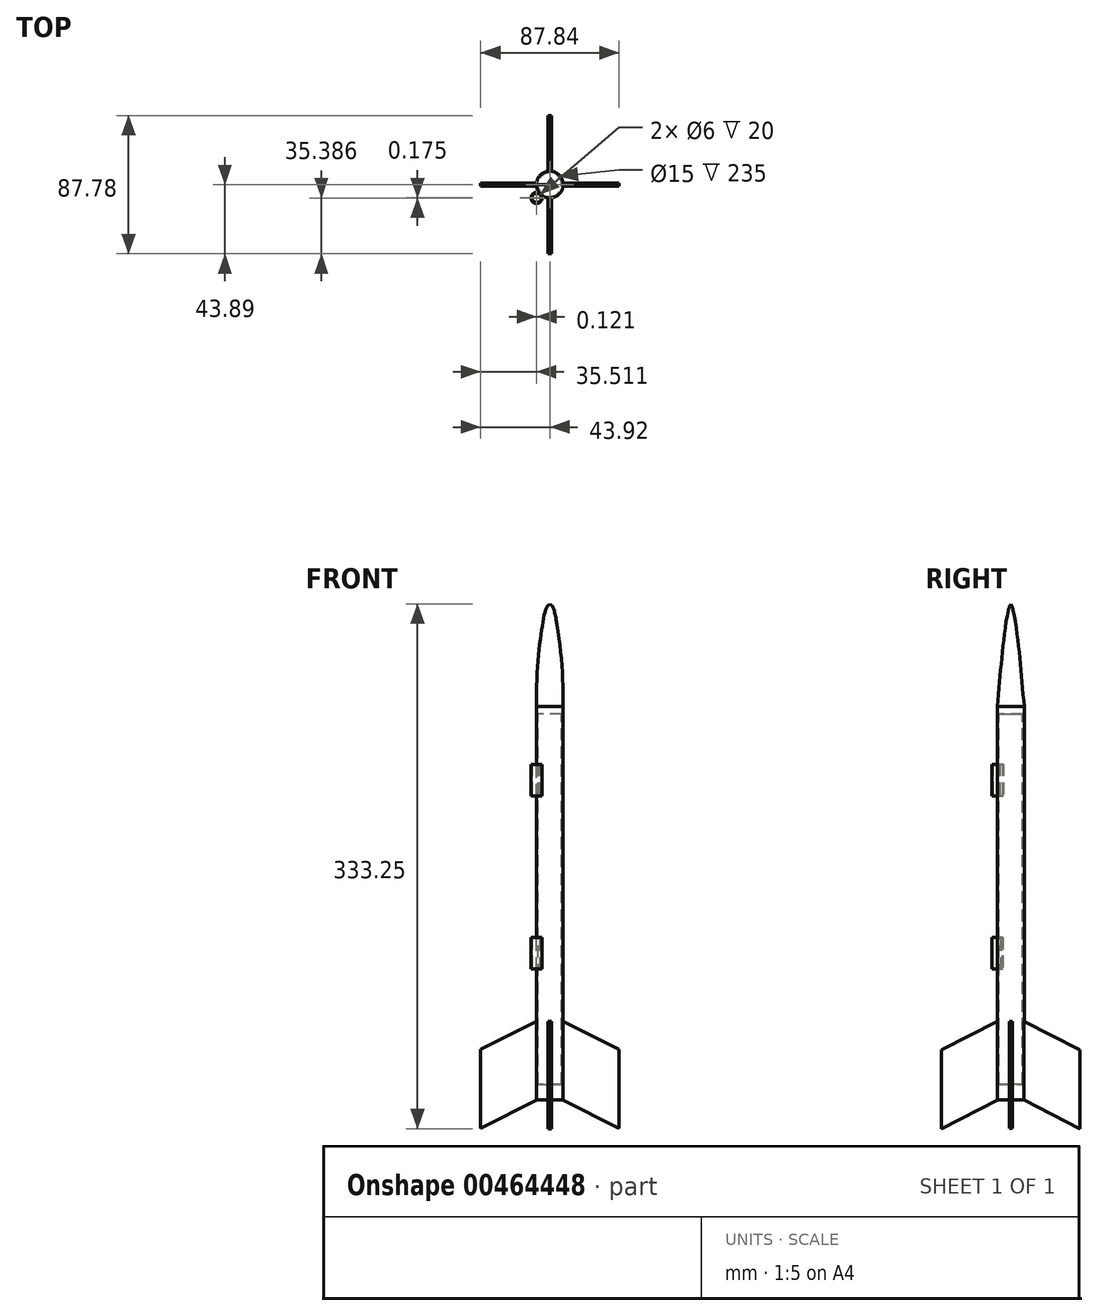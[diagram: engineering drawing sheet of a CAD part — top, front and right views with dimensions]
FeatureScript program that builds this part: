
annotation { "Feature Type Name" : "Feature", "Feature Type Description" : "" }
export const myFeature = defineFeature(function(context is Context, id is Id, definition is map)
    precondition{}
    {
        {
            var Q0;
            Q0=qCreatedBy(makeId("Front.planeOp"),FACE);
            var sketch = newSketch(context, id + "F0", { "sketchPlane" : qUnion([Q0])});
            skLineSegment(sketch, "E0", {"start": v(0, 0) * mm, "end": v(0, 70) * mm});
            skLineSegment(sketch, "E1", {"start": v(0, 0) * mm, "end": v(7.5, 0) * mm});
            skLineSegment(sketch, "E2", {"start": v(7.5, 0) * mm, "end": v(7.5, 5) * mm});
            skLineSegment(sketch, "E3", {"start": v(7.5, 5) * mm, "end": v(8.5, 5) * mm});
            skFitSpline(sketch, "E4", {"points": [v(0, 70) * mm, v(3.74, 61.8) * mm, v(8.5, 5) * mm], "startDerivative": vector(22.14, -9.96) * mm, "endDerivative": vector(-1.28, -102.15) * mm});
            skFitSpline(sketch, "E5.MirrorCS", {"points": [v(0, 70) * mm, v(-3.74, 61.8) * mm, v(-8.5, 5) * mm], "startDerivative": vector(-22.14, -9.96) * mm, "endDerivative": vector(1.28, -102.15) * mm});
            skLineSegment(sketch, "E6.MirrorCS", {"start": v(-7.5, 5) * mm, "end": v(-8.5, 5) * mm});
            skLineSegment(sketch, "E7.MirrorCS", {"start": v(-7.5, 0) * mm, "end": v(-7.5, 5) * mm});
            skLineSegment(sketch, "E8.MirrorCS", {"start": v(0, 0) * mm, "end": v(-7.5, 0) * mm});
            skSolve(sketch);
        }
        {
            var Q0;
            Q0=sQuery(id+"F0.wireOp",EDGE,"E3");
            cPlane(context, id + "F1", {"entities" : qUnion([Q0]), "cplaneType" : CPlaneType.LINE_ANGLE, "offset" : 25 * mm, "angle" : 90 * degree, "width" : 150 * mm, "height" : 150 * mm});
        }
        {
            var Q0;
            Q0=qCreatedBy(id+"F1.planeOp",FACE);
            var sketch = newSketch(context, id + "F2", { "sketchPlane" : qUnion([Q0])});
            skCircle(sketch, "E9", {"center": v(0, 0) * mm, "radius": 8.5 * mm});
            skSolve(sketch);
        }
        {
            var Q0;
            Q0=makeQuery(id+"F2.imprint","IMPRINT",FACE,{"disambiguationData":[TD([[makeQuery(id+"F2.imprint","IMPRINT",EDGE,{"derivedFrom":sQuery(id+"F2.wireOp",EDGE,"E9")}),1.0]])]});
            var Q1;
            Q1=sQuery(id+"F0.wireOp",VERTEX,"E5.MirrorCS.0.internal");
            var Q2;
            Q2=sQuery(id+"F0.wireOp",EDGE,"E4");
            var Q3;
            Q3=sQuery(id+"F0.wireOp",EDGE,"E5.MirrorCS");
            loft(context, id + "F3", {"addGuides" : true, "sheetProfilesArray" : [{ "sheetProfileEntities" : qUnion([Q0]) }, { "sheetProfileEntities" : qUnion([Q1]) }], "guidesArray" : [{ "guideEntities" : qUnion([Q2]), "guideDerivativeType" : LoftGuideDerivativeType.DEFAULT, "guideDerivativeMagnitude" : 1 }, { "guideEntities" : qUnion([Q3]), "guideDerivativeType" : LoftGuideDerivativeType.DEFAULT, "guideDerivativeMagnitude" : 1 }]});
        }
        {
            var Q0;
            Q0=qCreatedBy(makeId("Top.planeOp"),FACE);
            var sketch = newSketch(context, id + "F4", { "sketchPlane" : qUnion([Q0])});
            skCircle(sketch, "E10", {"center": v(0, 0) * mm, "radius": 7.5 * mm});
            skPoint(sketch, "E11", {"position": v(-6.24, 4.17) * mm});
            skSolve(sketch);
        }
        {
            var Q0;
            Q0=makeQuery(id+"F4.imprint","IMPRINT",FACE,{"disambiguationData":[TD([[makeQuery(id+"F4.imprint","IMPRINT",EDGE,{"derivedFrom":sQuery(id+"F4.wireOp",EDGE,"E10")}),1.0]])]});
            extrude(context, id + "F5", {"entities" : qUnion([Q0]), "operationType" : NewBodyOperationType.ADD, "depth" : 10 * mm});
        }
        {
            var Q0;
            Q0=makeQuery(id+"F3.opLoft","CAP_FACE",FACE,{"disambiguationData":[OSD([makeQuery(id+"F2.imprint","IMPRINT",FACE,{"disambiguationData":[TD([[makeQuery(id+"F2.imprint","IMPRINT",EDGE,{"derivedFrom":sQuery(id+"F2.wireOp",EDGE,"E9")}),1.0]])]})])],"isStart":true});
            extrude(context, id + "F6", {"entities" : qUnion([Q0]), "operationType" : NewBodyOperationType.ADD, "depth" : 250 * mm});
        }
        {
            var Q0;
            Q0=makeQuery(id+"F6.opExtrude","CAP_FACE",FACE,{"disambiguationData":[OSD([makeQuery(id+"F2.imprint","IMPRINT",FACE,{"disambiguationData":[TD([[makeQuery(id+"F2.imprint","IMPRINT",EDGE,{"derivedFrom":sQuery(id+"F2.wireOp",EDGE,"E9")}),1.0]])]})])],"isStart":false});
            var sketch = newSketch(context, id + "F7", { "sketchPlane" : qUnion([Q0])});
            skCircle(sketch, "E12", {"center": v(0, 0) * mm, "radius": 8.5 * mm});
            skPoint(sketch, "E13", {"position": v(-6.05, -5.97) * mm});
            skSolve(sketch);
        }
        {
            var Q0;
            Q0 = qSketchRegion(id + "F7", true);
            extrude(context, id + "F8", {"entities" : qUnion([Q0]), "operationType" : NewBodyOperationType.ADD, "oppositeDirection" : true, "depth" : 10 * mm});
        }
        {
            var Q0;
            Q0=qCreatedBy(makeId("Right.planeOp"),FACE);
            var sketch = newSketch(context, id + "F9", { "sketchPlane" : qUnion([Q0])});
            skLineSegment(sketch, "E14", {"start": v(0, 0) * mm, "end": v(0, -245) * mm});
            skLineSegment(sketch, "E15", {"start": v(0, -245) * mm, "end": v(8.3, -245) * mm});
            skLineSegment(sketch, "E16", {"start": v(8.3, -245) * mm, "end": v(8.3, -195) * mm});
            skLineSegment(sketch, "E17", {"start": v(8.3, -245) * mm, "end": v(43.9, -263.25) * mm});
            skLineSegment(sketch, "E18", {"start": v(43.9, -213.25) * mm, "end": v(43.9, -263.25) * mm});
            skLineSegment(sketch, "E19", {"start": v(8.3, -195) * mm, "end": v(43.9, -213.25) * mm});
            skLineSegment(sketch, "E20.MirrorCS", {"start": v(-8.3, -195) * mm, "end": v(-43.9, -213.25) * mm});
            skLineSegment(sketch, "E21.MirrorCS", {"start": v(-8.3, -245) * mm, "end": v(-8.3, -195) * mm});
            skLineSegment(sketch, "E22.MirrorCS", {"start": v(-43.9, -213.25) * mm, "end": v(-43.9, -263.25) * mm});
            skLineSegment(sketch, "E23.MirrorCS", {"start": v(-8.3, -245) * mm, "end": v(-43.9, -263.25) * mm});
            skLineSegment(sketch, "E24.MirrorCS", {"start": v(0, -245) * mm, "end": v(-8.3, -245) * mm});
            skSolve(sketch);
        }
        {
            var Q0;
            Q0=qCreatedBy(makeId("Front.planeOp"),FACE);
            var sketch = newSketch(context, id + "F10", { "sketchPlane" : qUnion([Q0])});
            skLineSegment(sketch, "E25", {"start": v(0, 0) * mm, "end": v(0, -245) * mm});
            skLineSegment(sketch, "E26", {"start": v(0, -245) * mm, "end": v(-8.2, -245) * mm});
            skLineSegment(sketch, "E27", {"start": v(-8.2, -245) * mm, "end": v(-8.2, -195) * mm});
            skLineSegment(sketch, "E28", {"start": v(-8.2, -195) * mm, "end": v(-43.92, -213) * mm});
            skLineSegment(sketch, "E29", {"start": v(-43.92, -213) * mm, "end": v(-43.92, -263) * mm});
            skLineSegment(sketch, "E30", {"start": v(-43.92, -263) * mm, "end": v(-8.2, -245) * mm});
            skLineSegment(sketch, "E31.MirrorCS", {"start": v(8.2, -195) * mm, "end": v(43.92, -213) * mm});
            skLineSegment(sketch, "E32.MirrorCS", {"start": v(43.92, -213) * mm, "end": v(43.92, -263) * mm});
            skLineSegment(sketch, "E33.MirrorCS", {"start": v(8.2, -245) * mm, "end": v(8.2, -195) * mm});
            skLineSegment(sketch, "E34.MirrorCS", {"start": v(43.92, -263) * mm, "end": v(8.2, -245) * mm});
            skLineSegment(sketch, "E35.MirrorCS", {"start": v(0, -245) * mm, "end": v(8.2, -245) * mm});
            skSolve(sketch);
        }
        {
            var Q0;
            Q0=sQuery(id+"F9.wireOp",EDGE,"E14");
            cPlane(context, id + "F11", {"entities" : qUnion([Q0]), "cplaneType" : CPlaneType.LINE_ANGLE, "offset" : 25 * mm, "angle" : 45 * degree, "width" : 150 * mm, "height" : 150 * mm});
        }
        {
            var Q0;
            Q0=qCreatedBy(id+"F11.planeOp",FACE);
            var sketch = newSketch(context, id + "F12", { "sketchPlane" : qUnion([Q0])});
            skLineSegment(sketch, "E36", {"start": v(8.42, 8.15) * mm, "end": v(8.42, -51.85) * mm});
            skLineSegment(sketch, "E37", {"start": v(8.42, -51.85) * mm, "end": v(15.42, -51.85) * mm});
            skLineSegment(sketch, "E38", {"start": v(15.42, -51.85) * mm, "end": v(15.42, -31.85) * mm});
            skLineSegment(sketch, "E39", {"start": v(15.42, -31.85) * mm, "end": v(8.42, -31.85) * mm});
            skLineSegment(sketch, "E40", {"start": v(8.42, -51.85) * mm, "end": v(8.42, -141.85) * mm});
            skLineSegment(sketch, "E41", {"start": v(8.42, -141.85) * mm, "end": v(8.42, -161.85) * mm});
            skLineSegment(sketch, "E42", {"start": v(8.42, -141.85) * mm, "end": v(15.42, -141.85) * mm});
            skLineSegment(sketch, "E43", {"start": v(15.42, -141.85) * mm, "end": v(15.42, -161.85) * mm});
            skLineSegment(sketch, "E44", {"start": v(15.42, -161.85) * mm, "end": v(8.42, -161.85) * mm});
            skSolve(sketch);
        }
        {
            var Q0;
            Q0=sQuery(id+"F12.wireOp",EDGE,"E44");
            cPlane(context, id + "F13", {"entities" : qUnion([Q0]), "cplaneType" : CPlaneType.LINE_ANGLE, "offset" : 25 * mm, "angle" : 0 * degree, "width" : 150 * mm, "height" : 150 * mm});
        }
        {
            var Q0;
            Q0=qCreatedBy(id+"F13.planeOp",FACE);
            var sketch = newSketch(context, id + "F14", { "sketchPlane" : qUnion([Q0])});
            skCircle(sketch, "E45", {"center": v(-8.4, -8.5) * mm, "radius": 3.5 * mm});
            skCircle(sketch, "E46", {"center": v(-8.4, -8.5) * mm, "radius": 3 * mm});
            skSolve(sketch);
        }
        {
            var Q0;
            Q0=makeQuery(id+"F14.imprint","IMPRINT",FACE,{"disambiguationData":[TD([[makeQuery(id+"F14.imprint","IMPRINT",EDGE,{"derivedFrom":sQuery(id+"F14.wireOp",EDGE,"E45")}),1.0]])]});
            extrude(context, id + "F15", {"entities" : qUnion([Q0]), "operationType" : NewBodyOperationType.ADD, "depth" : 20 * mm});
        }
        {
            var Q0;
            Q0=sQuery(id+"F12.wireOp",EDGE,"E37");
            cPlane(context, id + "F16", {"entities" : qUnion([Q0]), "cplaneType" : CPlaneType.LINE_ANGLE, "offset" : 25 * mm, "angle" : 0 * degree, "width" : 150 * mm, "height" : 150 * mm});
        }
        {
            var Q0;
            Q0=qCreatedBy(id+"F16.planeOp",FACE);
            var sketch = newSketch(context, id + "F17", { "sketchPlane" : qUnion([Q0])});
            skCircle(sketch, "E47", {"center": v(-8.29, 8.33) * mm, "radius": 3.5 * mm});
            skCircle(sketch, "E48", {"center": v(-8.29, 8.33) * mm, "radius": 3 * mm});
            skSolve(sketch);
        }
        {
            var Q0;
            Q0=makeQuery(id+"F17.imprint","IMPRINT",FACE,{"disambiguationData":[TD([[makeQuery(id+"F17.imprint","IMPRINT",EDGE,{"derivedFrom":sQuery(id+"F17.wireOp",EDGE,"E47")}),1.0]])]});
            extrude(context, id + "F18", {"entities" : qUnion([Q0]), "operationType" : NewBodyOperationType.ADD, "oppositeDirection" : true, "depth" : 20 * mm});
        }
        {
            var Q0;
            Q0=makeQuery(id+"F9.imprint","IMPRINT",FACE,{"disambiguationData":[TD([[makeQuery(id+"F9.imprint","IMPRINT",EDGE,{"derivedFrom":sQuery(id+"F9.wireOp",EDGE,"E16")}),-1.0]])]});
            var Q1;
            Q1=makeQuery(id+"F9.imprint","IMPRINT",FACE,{"disambiguationData":[TD([[makeQuery(id+"F9.imprint","IMPRINT",EDGE,{"derivedFrom":sQuery(id+"F9.wireOp",EDGE,"E20.MirrorCS")}),1.0]])]});
            extrude(context, id + "F19", {"entities" : qUnion([Q0, Q1]), "operationType" : NewBodyOperationType.ADD, "endBound" : BoundingType.SYMMETRIC, "depth" : 2 * mm});
        }
        {
            var Q0;
            Q0=makeQuery(id+"F10.imprint","IMPRINT",FACE,{"disambiguationData":[TD([[makeQuery(id+"F10.imprint","IMPRINT",EDGE,{"derivedFrom":sQuery(id+"F10.wireOp",EDGE,"E31.MirrorCS")}),-1.0]])]});
            var Q1;
            Q1=makeQuery(id+"F10.imprint","IMPRINT",FACE,{"disambiguationData":[TD([[makeQuery(id+"F10.imprint","IMPRINT",EDGE,{"derivedFrom":sQuery(id+"F10.wireOp",EDGE,"E27")}),1.0]])]});
            extrude(context, id + "F20", {"entities" : qUnion([Q0, Q1]), "operationType" : NewBodyOperationType.ADD, "endBound" : BoundingType.SYMMETRIC, "depth" : 2 * mm});
        }
    });
